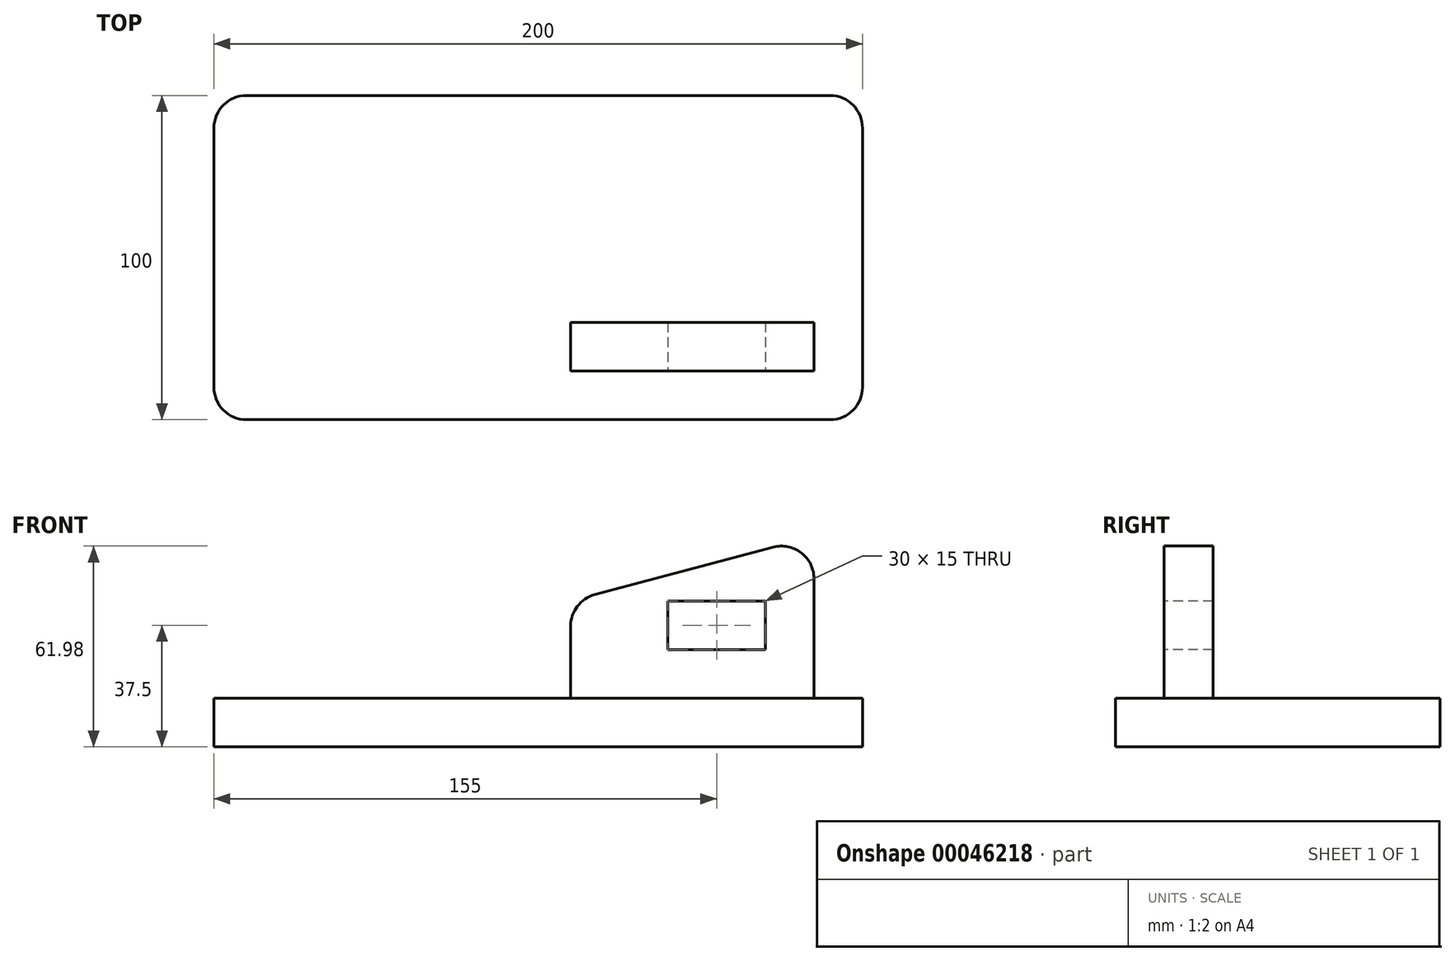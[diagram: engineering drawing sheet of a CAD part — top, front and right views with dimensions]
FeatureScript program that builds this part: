
annotation { "Feature Type Name" : "Feature", "Feature Type Description" : "" }
export const myFeature = defineFeature(function(context is Context, id is Id, definition is map)
    precondition{}
    {
        {
            var Q0;
            Q0=qCreatedBy(makeId("Top.planeOp"),FACE);
            var sketch = newSketch(context, id + "F0", { "sketchPlane" : qUnion([Q0])});
            skLineSegment(sketch, "E0.bottom", {"start": v(0, 0) * mm, "end": v(200, 0) * mm});
            skLineSegment(sketch, "E0.top", {"start": v(0, 100) * mm, "end": v(200, 100) * mm});
            skLineSegment(sketch, "E0.left", {"start": v(0, 0) * mm, "end": v(0, 100) * mm});
            skLineSegment(sketch, "E0.right", {"start": v(200, 0) * mm, "end": v(200, 100) * mm});
            skSolve(sketch);
        }
        {
            var Q0;
            Q0=makeQuery(id+"F0.imprint","IMPRINT",FACE,{"disambiguationData":[TD([[makeQuery(id+"F0.imprint","IMPRINT",EDGE,{"derivedFrom":sQuery(id+"F0.wireOp",EDGE,"E0.bottom")}),1.0]])]});
            extrude(context, id + "F1", {"entities" : qUnion([Q0]), "depth" : 15 * mm});
        }
        {
            var Q0;
            Q0=makeQuery(id+"F1.opExtrude","SWEPT_FACE",FACE,{"disambiguationData":[OSD([sQuery(id+"F0.wireOp",EDGE,"E0.bottom")])]});
            cPlane(context, id + "F2", {"entities" : qUnion([Q0]), "cplaneType" : CPlaneType.OFFSET, "offset" : 15 * mm, "oppositeDirection" : true, "width" : 150 * mm, "height" : 150 * mm});
        }
        {
            var Q0;
            Q0=qCreatedBy(id+"F2.planeOp",FACE);
            var sketch = newSketch(context, id + "F3", { "sketchPlane" : qUnion([Q0])});
            skLineSegment(sketch, "E1", {"start": v(185, 15) * mm, "end": v(185, 65) * mm});
            skLineSegment(sketch, "E2", {"start": v(185, 65) * mm, "end": v(110, 45) * mm});
            skLineSegment(sketch, "E3", {"start": v(110, 45) * mm, "end": v(110, 15) * mm});
            skLineSegment(sketch, "E4", {"start": v(110, 15) * mm, "end": v(185, 15) * mm});
            skLineSegment(sketch, "E5.bottom", {"start": v(170, 30) * mm, "end": v(140, 30) * mm});
            skLineSegment(sketch, "E5.top", {"start": v(170, 45) * mm, "end": v(140, 45) * mm});
            skLineSegment(sketch, "E5.left", {"start": v(170, 30) * mm, "end": v(170, 45) * mm});
            skLineSegment(sketch, "E5.right", {"start": v(140, 30) * mm, "end": v(140, 45) * mm});
            skSolve(sketch);
        }
        {
            var Q0;
            Q0=makeQuery(id+"F3.imprint","IMPRINT",FACE,{"disambiguationData":[TD([[makeQuery(id+"F3.imprint","IMPRINT",EDGE,{"derivedFrom":sQuery(id+"F3.wireOp",EDGE,"E1")}),1.0]])]});
            extrude(context, id + "F4", {"entities" : qUnion([Q0]), "operationType" : NewBodyOperationType.ADD, "oppositeDirection" : true, "depth" : 15 * mm});
        }
        {
            var Q0;
            Q0=makeQuery(id+"F1.opExtrude","SWEPT_EDGE",EDGE,{"disambiguationData":[OSD([sQuery(id+"F0.wireOp",EDGE,"E0.bottom"),sQuery(id+"F0.wireOp",EDGE,"E0.left")])]});
            var Q1;
            Q1=makeQuery(id+"F1.opExtrude","SWEPT_EDGE",EDGE,{"disambiguationData":[OSD([sQuery(id+"F0.wireOp",EDGE,"E0.top"),sQuery(id+"F0.wireOp",EDGE,"E0.left")])]});
            var Q2;
            Q2=makeQuery(id+"F1.opExtrude","SWEPT_EDGE",EDGE,{"disambiguationData":[OSD([sQuery(id+"F0.wireOp",EDGE,"E0.bottom"),sQuery(id+"F0.wireOp",EDGE,"E0.right")])]});
            var Q3;
            Q3=makeQuery(id+"F4.opExtrude","SWEPT_EDGE",EDGE,{"disambiguationData":[OSD([sQuery(id+"F3.wireOp",EDGE,"E2"),sQuery(id+"F3.wireOp",EDGE,"E3")])]});
            var Q4;
            Q4=makeQuery(id+"F4.opExtrude","SWEPT_EDGE",EDGE,{"disambiguationData":[OSD([sQuery(id+"F3.wireOp",EDGE,"E1"),sQuery(id+"F3.wireOp",EDGE,"E2")])]});
            var Q5;
            Q5=makeQuery(id+"F1.opExtrude","SWEPT_EDGE",EDGE,{"disambiguationData":[OSD([sQuery(id+"F0.wireOp",EDGE,"E0.top"),sQuery(id+"F0.wireOp",EDGE,"E0.right")])]});
            fillet(context, id + "F5", {"entities" : qUnion([Q0, Q1, Q2, Q3, Q4, Q5]), "radius" : 10 * mm, "tangentPropagation" : true, "allowEdgeOverflow" : false});
        }
    });
